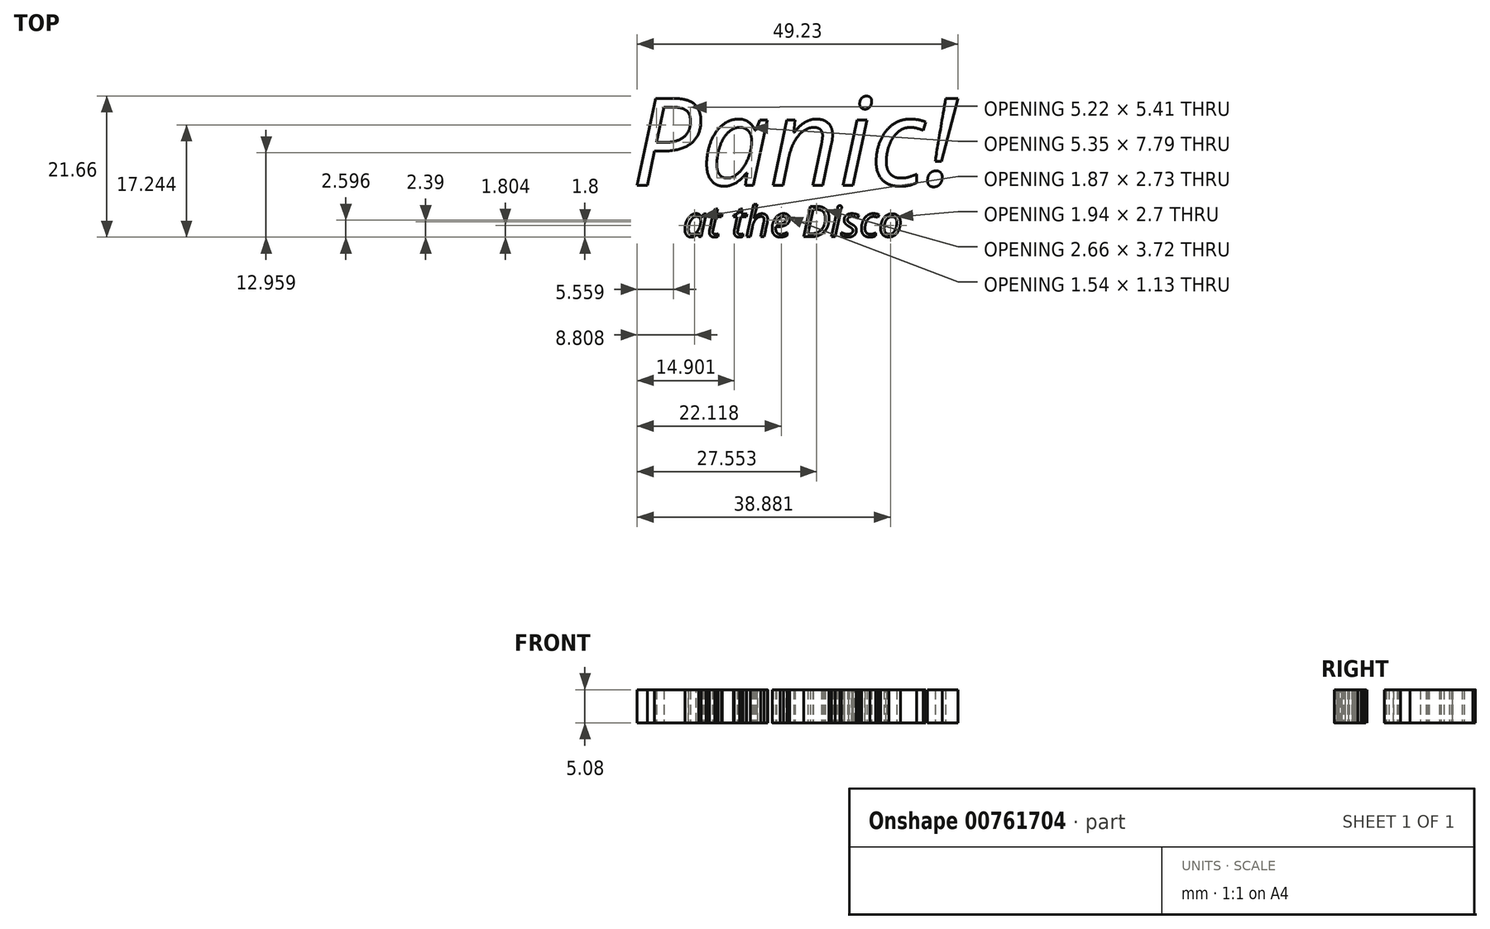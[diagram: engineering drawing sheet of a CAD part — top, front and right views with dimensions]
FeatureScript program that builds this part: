
annotation { "Feature Type Name" : "Feature", "Feature Type Description" : "" }
export const myFeature = defineFeature(function(context is Context, id is Id, definition is map)
    precondition{}
    {
        {
            var Q0;
            Q0=qCreatedBy(makeId("Top.planeOp"),FACE);
            var sketch = newSketch(context, id + "F0", { "sketchPlane" : qUnion([Q0])});
            skText(sketch, "E0", { "text": "Panic!", "fontName": "OpenSans-Italic.ttf"});
            skText(sketch, "E1", { "text": "at the Disco", "fontName": "OpenSans-Italic.ttf"});
            const initialGuessF0  = {"E0": [-0.06214, 0.00792, 1, 0, 0.01342], "E1": [-0.05435, 0, 1, 0, 0.0047]};
            skSetInitialGuess(sketch, initialGuessF0);
            skSolve(sketch);
        }
        {
            var Q0;
            Q0 = qSketchRegion(id + "F0", true);
            extrude(context, id + "F1", {"entities" : qUnion([Q0]), "depth" : 5.08 * mm, "offsetDistance" : 25.4 * mm});
        }
    });
